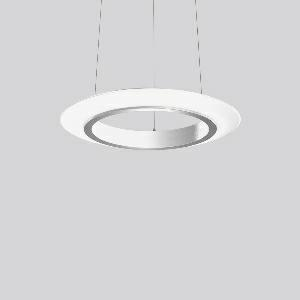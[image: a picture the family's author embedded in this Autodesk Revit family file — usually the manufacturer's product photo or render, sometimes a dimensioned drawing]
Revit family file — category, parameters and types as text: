
# Revit family: ring_of_fire_p_311669_004_1_76_1b6e
name_source: partatom
category: Lighting Fixtures
units: mm (PartAtom-declared; Revit-internal decimal feet)

## family parameters
Cut with Voids When Loaded = No
Host = Face
Light Source = No
Part Type = Normal
Room Calculation Point = No
Round Connector Dimension = Use Diameter
Shared = No

## types (1)
- RING OF FIRE P (1 x LED Modul 840, 2900 lm, 4000)
    Apparent Load = 28 VA
    CIE Flux Codes = 43 72 90 56 100
    Color Rendering = 80
    Color Temperature = 4000
    Default Elevation = 1800 mm
    Description = Series: RING OF FIRE
A uniquely shaped pendant luminaire with elliptical glass. Supporting ring made of anodised aluminium. Canopy aluminium anodised. Opal glass: mouth-blown, satin finish. Suitable for pendant. 3-point steel cable suspension, steplessly adjustable. Special lengths available on request. For pendant lengths of up to 2 m, power is supplied through a suspension cable. For pendant lengths of 2 m and more, power must be supplied through a separate cable. Converter integrated in the canopy. TouchDim sensor capable. Light and/or presence sensors can be integrated. 
Colour: anodised aluminium
Diameter: 495 mm
Height: 55 mm
Suspension length: 500-1200 mm
Lamp: LED
Socket: without socket
Colour temperature: 4000K
Colour rendering index (CRI): 80
System power: 28 W
Rated luminous flux: 2900 lm
Luminous efficiency: 104 lm/W
Control gear: Converter, dimmable, DALI
Protection class: I
Type of protection: IP 20
    Height = 55 mm
    Lamp = 1 x LED Modul 840
    Lamp Light Flux = 2900 lm
    Lamp count = 1
    Length = 495 mm
    Lifetime = 50000 h
    Luminous efficacy = 104 lm/W
    Manufacturer = RZB
    ModVariant = No
    Model = 311669.004.1.76
    Mounting Place = Ceiling
    Mounting Type = Pendant
    Number of Poles = 1
    OnlyDefault = Yes
    Power Factor = 1
    Product Name = RING OF FIRE P
    Product group = Pendant luminaires
    ProductGroupID = 902
    Protection Class = Protection class I
    Protection Degree = IP 20
    RLX_Detail_Level = 1
    RLX_Emergency_Light_Flux = 0 lm
    RLX_Emergency_Type = 0
    RLX_Emergency_Type_DB = No
    RlxData = <blob elided: 38581 chars, md5=17c08209>
    Socket = socket
    Standby Power = 0 W
    System Light Flux = 2900 lm
    System Power = 28 W
    Type Comments = Product without accessories
    Type Image = 311669.004.jpg
    URL = http://relux.com
    VarID = ---
    Voltage = 230 V
    Voltage Range = 220-240 V
    Weight = 0.00 kg
    Width = 0 mm  [stored 0 ft]

note: [stored X ft] marks values corroborated as IEEE doubles in the binary element streams (Revit-internal decimal feet)

## geometry (parser evidence)
native form markers: Blend x4, Sweep x13
no freeform markers — native parametric forms only
